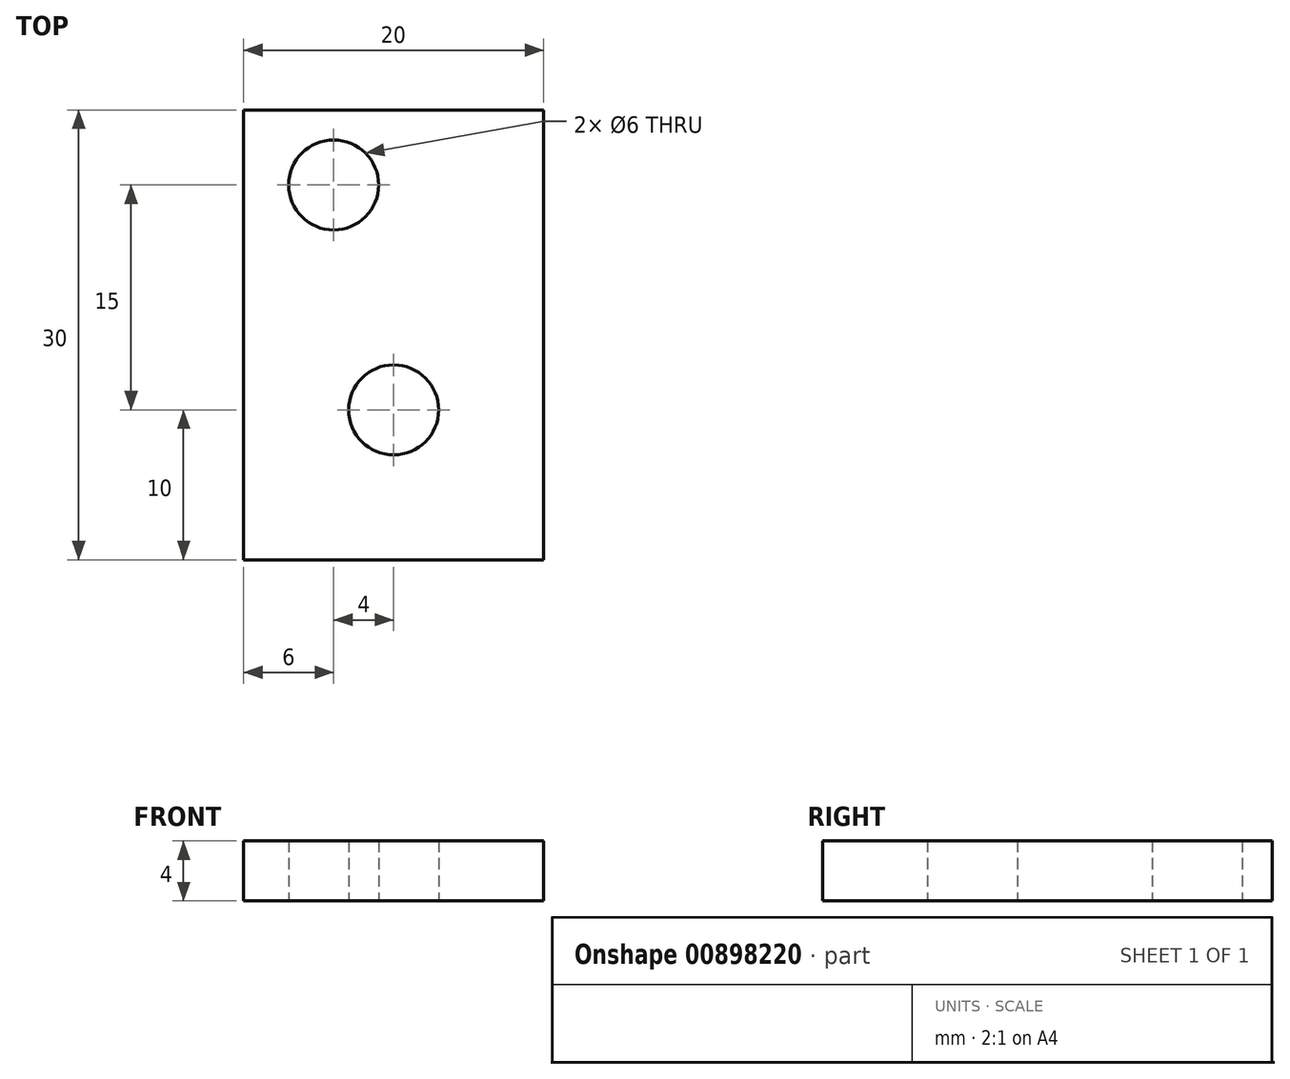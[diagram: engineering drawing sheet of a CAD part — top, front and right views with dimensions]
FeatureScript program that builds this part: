
annotation { "Feature Type Name" : "Feature", "Feature Type Description" : "" }
export const myFeature = defineFeature(function(context is Context, id is Id, definition is map)
    precondition{}
    {
        {
            var Q0;
            Q0=qCreatedBy(makeId("Top.planeOp"),FACE);
            var sketch = newSketch(context, id + "F0", { "sketchPlane" : qUnion([Q0])});
            skLineSegment(sketch, "E0.bottom", {"start": v(-10, 15) * mm, "end": v(10, 15) * mm});
            skLineSegment(sketch, "E0.top", {"start": v(-10, -15) * mm, "end": v(10, -15) * mm});
            skLineSegment(sketch, "E0.left", {"start": v(-10, 15) * mm, "end": v(-10, -15) * mm});
            skLineSegment(sketch, "E0.right", {"start": v(10, 15) * mm, "end": v(10, -15) * mm});
            skPoint(sketch, "E0.middle", {"position": v(0, 0) * mm});
            skPoint(sketch, "E1", {"position": v(-4, 10) * mm});
            skLineSegment(sketch, "E2", {"start": v(0, -15) * mm, "end": v(0, -5) * mm});
            skSolve(sketch);
        }
        {
            var Q0;
            Q0 = qSketchRegion(id + "F0", true);
            extrude(context, id + "F1", {"entities" : qUnion([Q0]), "depth" : 4 * mm, "offsetDistance" : 25 * mm});
        }
        {
            var Q0;
            Q0=sQuery(id+"F0.wireOp",VERTEX,"E1");
            var Q1;
            Q1=makeQuery(id+"F1.opExtrude","SWEPT_BODY",BODY,{"disambiguationData":[OSD([sQuery(id+"F0.wireOp",EDGE,"E0.bottom"),sQuery(id+"F0.wireOp",EDGE,"E0.top"),sQuery(id+"F0.wireOp",EDGE,"E0.left"),sQuery(id+"F0.wireOp",EDGE,"E0.right")])]});
            hole(context, id + "F2", {"style" : HoleStyle.SIMPLE, "endStyle" : HoleEndStyle.THROUGH, "oppositeDirection" : true, "holeDiameter" : 6 * mm, "majorDiameter" : 5 * mm, "isTappedThrough" : true, "tappedDepth" : 12 * mm, "tapClearance" : 3, "locations" : qUnion([Q0]), "scope" : qUnion([Q1])});
        }
        {
            var Q0;
            Q0=sQuery(id+"F0.wireOp",VERTEX,"E2.end");
            var Q1;
            Q1=makeQuery(id+"F1.opExtrude","SWEPT_BODY",BODY,{"disambiguationData":[OSD([sQuery(id+"F0.wireOp",EDGE,"E0.bottom"),sQuery(id+"F0.wireOp",EDGE,"E0.top"),sQuery(id+"F0.wireOp",EDGE,"E0.left"),sQuery(id+"F0.wireOp",EDGE,"E0.right")])]});
            hole(context, id + "F3", {"style" : HoleStyle.SIMPLE, "endStyle" : HoleEndStyle.THROUGH, "oppositeDirection" : true, "holeDiameter" : 6 * mm, "majorDiameter" : 5 * mm, "isTappedThrough" : true, "tappedDepth" : 12 * mm, "tapClearance" : 3, "locations" : qUnion([Q0]), "scope" : qUnion([Q1])});
        }
    });
